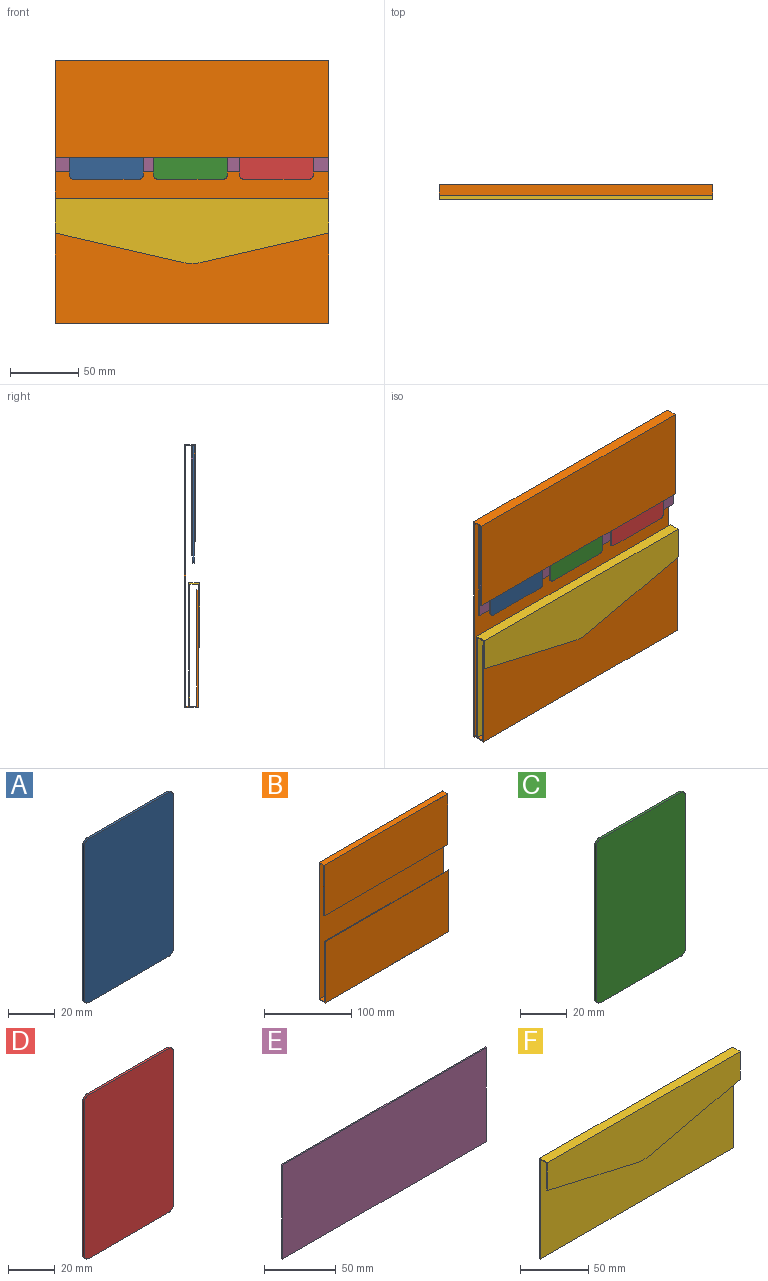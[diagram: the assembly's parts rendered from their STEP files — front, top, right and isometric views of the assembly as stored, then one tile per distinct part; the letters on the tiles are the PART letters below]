
ASSEMBLY  parts=6 mates=11
PART A: 10 faces, bbox 54x1x85.6 mm
  f0: plane 48x1mm, normal (0,0,1), area 48mm2, adj f4,f5,f6,f9
  f1: plane 79.6x1mm, normal (-1,0,0), area 79.6mm2, adj f4,f5,f6,f7
  f2: plane 48x1mm, normal (0,0,-1), area 48mm2, adj f4,f5,f7,f8
  f3: plane 79.6x1mm, normal (1,0,0), area 79.6mm2, adj f4,f5,f8,f9
  f4: plane 85.6x54mm, normal (0,-1,0), area 4614.7mm2, adj f0,f1,f2,f3,f6,f7,f8,f9
  f5: plane 85.6x54mm, normal (0,1,0), area 4614.7mm2, adj f0,f1,f2,f3,f6,f7,f8,f9
  f6: cylinder r=3mm len=3mm, axis (0,-1,0), area 4.7mm2, adj f0,f1,f4,f5
  f7: cylinder r=3mm len=3mm, axis (0,1,0), area 4.7mm2, adj f1,f2,f4,f5
  f8: cylinder r=3mm len=3mm, axis (0,-1,0), area 4.7mm2, adj f2,f3,f4,f5
  f9: cylinder r=3mm len=3mm, axis (0,1,0), area 4.7mm2, adj f0,f3,f4,f5
PART B: 14 faces, bbox 200x10x192 mm
  f0: plane 200x70mm, normal (0,1,0), area 14000mm2, adj f1,f11,f12,f13
  f1: plane 200x6mm, normal (0,0,-1), area 1200mm2, adj f0,f2,f12,f13
  f2: plane 200x190mm, normal (0,-1,0), area 38000mm2, adj f1,f3,f12,f13
  f3: plane 200x8mm, normal (0,0,1), area 1600mm2, adj f2,f4,f12,f13
  f4: plane 200x85mm, normal (0,1,0), area 17000mm2, adj f3,f5,f12,f13
  f5: plane 200x1mm, normal (0,0,1), area 200mm2, adj f4,f6,f12,f13
  f6: plane 200x86mm, normal (0,-1,0), area 17200mm2, adj f5,f7,f12,f13
  f7: plane 200x10mm, normal (0,0,-1), area 2000mm2, adj f6,f8,f12,f13
  f8: plane 200x192mm, normal (0,1,0), area 38400mm2, adj f7,f9,f12,f13
  f9: plane 200x8mm, normal (0,0,1), area 1600mm2, adj f8,f10,f12,f13
  f10: plane 200x71mm, normal (0,-1,0), area 14200mm2, adj f9,f11,f12,f13
  f11: plane 200x1mm, normal (0,0,-1), area 200mm2, adj f0,f10,f12,f13
  f12: plane 192x10mm, normal (-1,0,0), area 363mm2, adj f0,f1,f2,f3,f4,f5,f6,f7
  f13: plane 192x10mm, normal (1,0,0), area 363mm2, adj f0,f1,f2,f3,f4,f5,f6,f7
PART C: 10 faces, bbox 54x1x85.6 mm
  f0: plane 48x1mm, normal (0,0,1), area 48mm2, adj f4,f5,f6,f9
  f1: plane 79.6x1mm, normal (-1,0,0), area 79.6mm2, adj f4,f5,f6,f7
  f2: plane 48x1mm, normal (0,0,-1), area 48mm2, adj f4,f5,f7,f8
  f3: plane 79.6x1mm, normal (1,0,0), area 79.6mm2, adj f4,f5,f8,f9
  f4: plane 85.6x54mm, normal (0,-1,0), area 4614.7mm2, adj f0,f1,f2,f3,f6,f7,f8,f9
  f5: plane 85.6x54mm, normal (0,1,0), area 4614.7mm2, adj f0,f1,f2,f3,f6,f7,f8,f9
  f6: cylinder r=3mm len=3mm, axis (0,-1,0), area 4.7mm2, adj f0,f1,f4,f5
  f7: cylinder r=3mm len=3mm, axis (0,1,0), area 4.7mm2, adj f1,f2,f4,f5
  f8: cylinder r=3mm len=3mm, axis (0,-1,0), area 4.7mm2, adj f2,f3,f4,f5
  f9: cylinder r=3mm len=3mm, axis (0,1,0), area 4.7mm2, adj f0,f3,f4,f5
PART D: 10 faces, bbox 54x1x85.6 mm
  f0: plane 48x1mm, normal (0,0,1), area 48mm2, adj f4,f5,f6,f9
  f1: plane 79.6x1mm, normal (-1,0,0), area 79.6mm2, adj f4,f5,f6,f7
  f2: plane 48x1mm, normal (0,0,-1), area 48mm2, adj f4,f5,f7,f8
  f3: plane 79.6x1mm, normal (1,0,0), area 79.6mm2, adj f4,f5,f8,f9
  f4: plane 85.6x54mm, normal (0,-1,0), area 4614.7mm2, adj f0,f1,f2,f3,f6,f7,f8,f9
  f5: plane 85.6x54mm, normal (0,1,0), area 4614.7mm2, adj f0,f1,f2,f3,f6,f7,f8,f9
  f6: cylinder r=3mm len=3mm, axis (0,-1,0), area 4.7mm2, adj f0,f1,f4,f5
  f7: cylinder r=3mm len=3mm, axis (0,1,0), area 4.7mm2, adj f1,f2,f4,f5
  f8: cylinder r=3mm len=3mm, axis (0,-1,0), area 4.7mm2, adj f2,f3,f4,f5
  f9: cylinder r=3mm len=3mm, axis (0,1,0), area 4.7mm2, adj f0,f3,f4,f5
PART E: 6 faces, bbox 200x1x80 mm
  f0: plane 200x1mm, normal (0,0,1), area 200mm2, adj f1,f3,f4,f5
  f1: plane 80x1mm, normal (-1,0,0), area 80mm2, adj f0,f2,f4,f5
  f2: plane 200x1mm, normal (0,0,-1), area 200mm2, adj f1,f3,f4,f5
  f3: plane 80x1mm, normal (1,0,0), area 80mm2, adj f0,f2,f4,f5
  f4: plane 200x80mm, normal (0,-1,0), area 16000mm2, adj f0,f1,f2,f3
  f5: plane 200x80mm, normal (0,1,0), area 16000mm2, adj f0,f1,f2,f3
PART F: 12 faces, bbox 200x8x90 mm
  f0: plane 200x47.22mm, normal (0,-1,0), area 7296.5mm2, adj f4,f7,f8,f9,f10,f11
  f1: plane 200x89mm, normal (0,-1,0), area 17800mm2, adj f2,f6,f7,f8
  f2: plane 200x1mm, normal (0,0,-1), area 200mm2, adj f1,f3,f7,f8
  f3: plane 200x90mm, normal (0,1,0), area 18000mm2, adj f2,f4,f7,f8
  f4: plane 200x8mm, normal (0,0,1), area 1600mm2, adj f0,f3,f7,f8
  f5: plane 200x46.22mm, normal (0,1,0), area 7096.5mm2, adj f6,f7,f8,f9,f10,f11
  f6: plane 200x6mm, normal (0,0,-1), area 1200mm2, adj f1,f5,f7,f8
  f7: plane 90x8mm, normal (1,0,0), area 121mm2, adj f0,f1,f2,f3,f4,f5,f6,f10
  f8: plane 90x8mm, normal (-1,0,0), area 121mm2, adj f0,f1,f2,f3,f4,f5,f6,f9
  f9: plane 93.28x21.45mm, normal (-0.22,0,-0.97), area 95.7mm2, adj f0,f5,f8,f11
  f10: plane 93.28x21.45mm, normal (0.22,0,-0.97), area 95.7mm2, adj f0,f5,f7,f11
  f11: cylinder r=30mm len=13.45mm, axis (0,-1,0), area 13.6mm2, adj f0,f5,f9,f10
PLACE A t=(-37.69,-3.94,180.07)mm
PLACE B t=(191.89,1.06,85.07)mm
PLACE C t=(93.74,-3.94,180.07)mm
PLACE D t=(226.56,-3.94,180.07)mm
PLACE E t=(91.89,-2.94,180.07)mm
PLACE F t=(91.89,-1.94,-9.93)mm
MATE planar D.f8 <-> C.f4  axis (0,-1,0) through (277.56,-4.94,97.47)mm
MATE planar E.f0 <-> B.f1  axis (0,0,1) through (191.89,-3.44,180.07)mm
MATE planar E.f3 <-> B.f13  axis (1,0,0) through (291.89,-3.44,140.07)mm
MATE planar D.f4 <-> A.f4  axis (0,-1,0) through (253.56,-4.94,137.27)mm
MATE planar F.f7 <-> B.f13  axis (1,0,0) through (291.89,-3.06,43.99)mm
MATE planar D.f5 <-> E.f4  axis (0,1,0) through (253.56,-3.94,137.27)mm
MATE planar D.f2 <-> A.f2  axis (0,0,-1) through (253.56,-4.44,94.47)mm
MATE planar D.f4 <-> B.f0  axis (0,-1,0) through (253.56,-4.94,137.27)mm
MATE planar B.f1 <-> D.f0  axis (0,0,-1) through (191.89,-1.94,180.07)mm
MATE planar F.f2 <-> B.f3  axis (0,0,-1) through (191.89,-1.44,-9.93)mm
MATE planar D.f2 <-> C.f2  axis (0,0,-1) through (253.56,-4.44,94.47)mm
